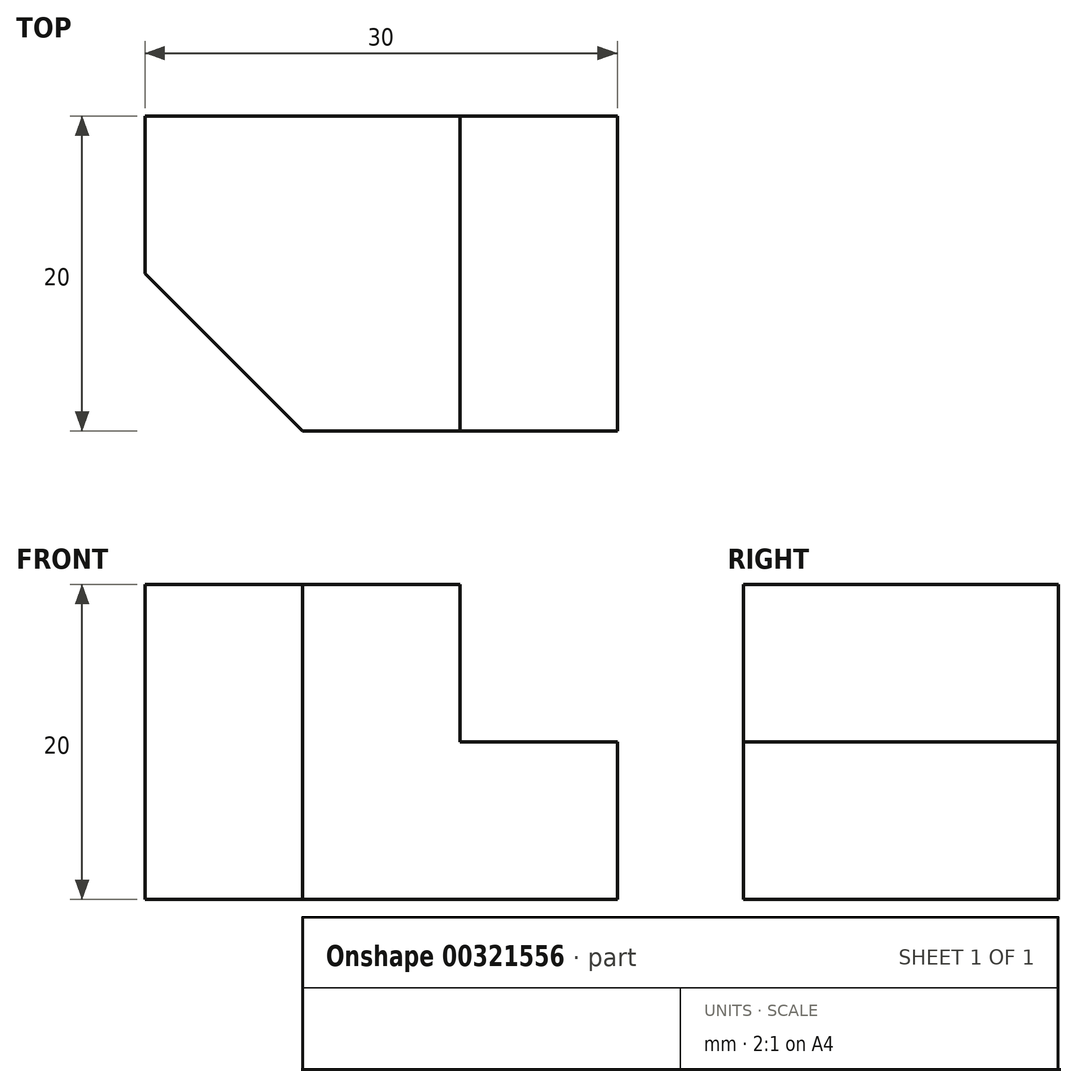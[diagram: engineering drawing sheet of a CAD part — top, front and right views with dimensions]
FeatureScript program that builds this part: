
annotation { "Feature Type Name" : "Feature", "Feature Type Description" : "" }
export const myFeature = defineFeature(function(context is Context, id is Id, definition is map)
    precondition{}
    {
        {
            var Q0;
            Q0=qCreatedBy(makeId("Front.planeOp"),FACE);
            var sketch = newSketch(context, id + "F0", { "sketchPlane" : qUnion([Q0])});
            skLineSegment(sketch, "E0", {"start": v(0, 0) * mm, "end": v(0, 20) * mm});
            skLineSegment(sketch, "E1", {"start": v(0, 20) * mm, "end": v(30, 20) * mm});
            skLineSegment(sketch, "E2", {"start": v(30, 20) * mm, "end": v(30, 0) * mm});
            skLineSegment(sketch, "E3", {"start": v(30, 0) * mm, "end": v(0, 0) * mm});
            skSolve(sketch);
        }
        {
            var Q0;
            Q0 = qSketchRegion(id + "F0", true);
            extrude(context, id + "F1", {"entities" : qUnion([Q0]), "depth" : 20 * mm});
        }
        {
            var Q0;
            Q0=makeQuery(id+"F1.opExtrude","SWEPT_FACE",FACE,{"disambiguationData":[OSD([sQuery(id+"F0.wireOp",EDGE,"E1")])]});
            var sketch = newSketch(context, id + "F2", { "sketchPlane" : qUnion([Q0])});
            skLineSegment(sketch, "E4", {"start": v(0, -10) * mm, "end": v(0, -20) * mm});
            skLineSegment(sketch, "E5", {"start": v(0, -20) * mm, "end": v(10, -20) * mm});
            skLineSegment(sketch, "E6", {"start": v(10, -20) * mm, "end": v(0, -10) * mm});
            skSolve(sketch);
        }
        {
            var Q0;
            Q0 = qSketchRegion(id + "F2", true);
            extrude(context, id + "F3", {"entities" : qUnion([Q0]), "operationType" : NewBodyOperationType.REMOVE, "endBound" : BoundingType.THROUGH_ALL, "oppositeDirection" : true, "depth" : 25 * mm});
        }
        {
            var Q0;
            Q0=makeQuery(id+"F1.opExtrude","CAP_FACE",FACE,{"disambiguationData":[OSD([sQuery(id+"F0.wireOp",EDGE,"E0"),sQuery(id+"F0.wireOp",EDGE,"E1"),sQuery(id+"F0.wireOp",EDGE,"E2"),sQuery(id+"F0.wireOp",EDGE,"E3")])],"isStart":false});
            var sketch = newSketch(context, id + "F4", { "sketchPlane" : qUnion([Q0])});
            skLineSegment(sketch, "E7", {"start": v(30, 20) * mm, "end": v(20, 20) * mm});
            skLineSegment(sketch, "E8", {"start": v(20, 20) * mm, "end": v(20, 10) * mm});
            skLineSegment(sketch, "E9", {"start": v(20, 10) * mm, "end": v(30, 10) * mm});
            skLineSegment(sketch, "E10", {"start": v(30, 10) * mm, "end": v(30, 20) * mm});
            skSolve(sketch);
        }
        {
            var Q0;
            Q0 = qSketchRegion(id + "F4", true);
            extrude(context, id + "F5", {"entities" : qUnion([Q0]), "operationType" : NewBodyOperationType.REMOVE, "endBound" : BoundingType.THROUGH_ALL, "oppositeDirection" : true, "depth" : 25 * mm});
        }
    });
